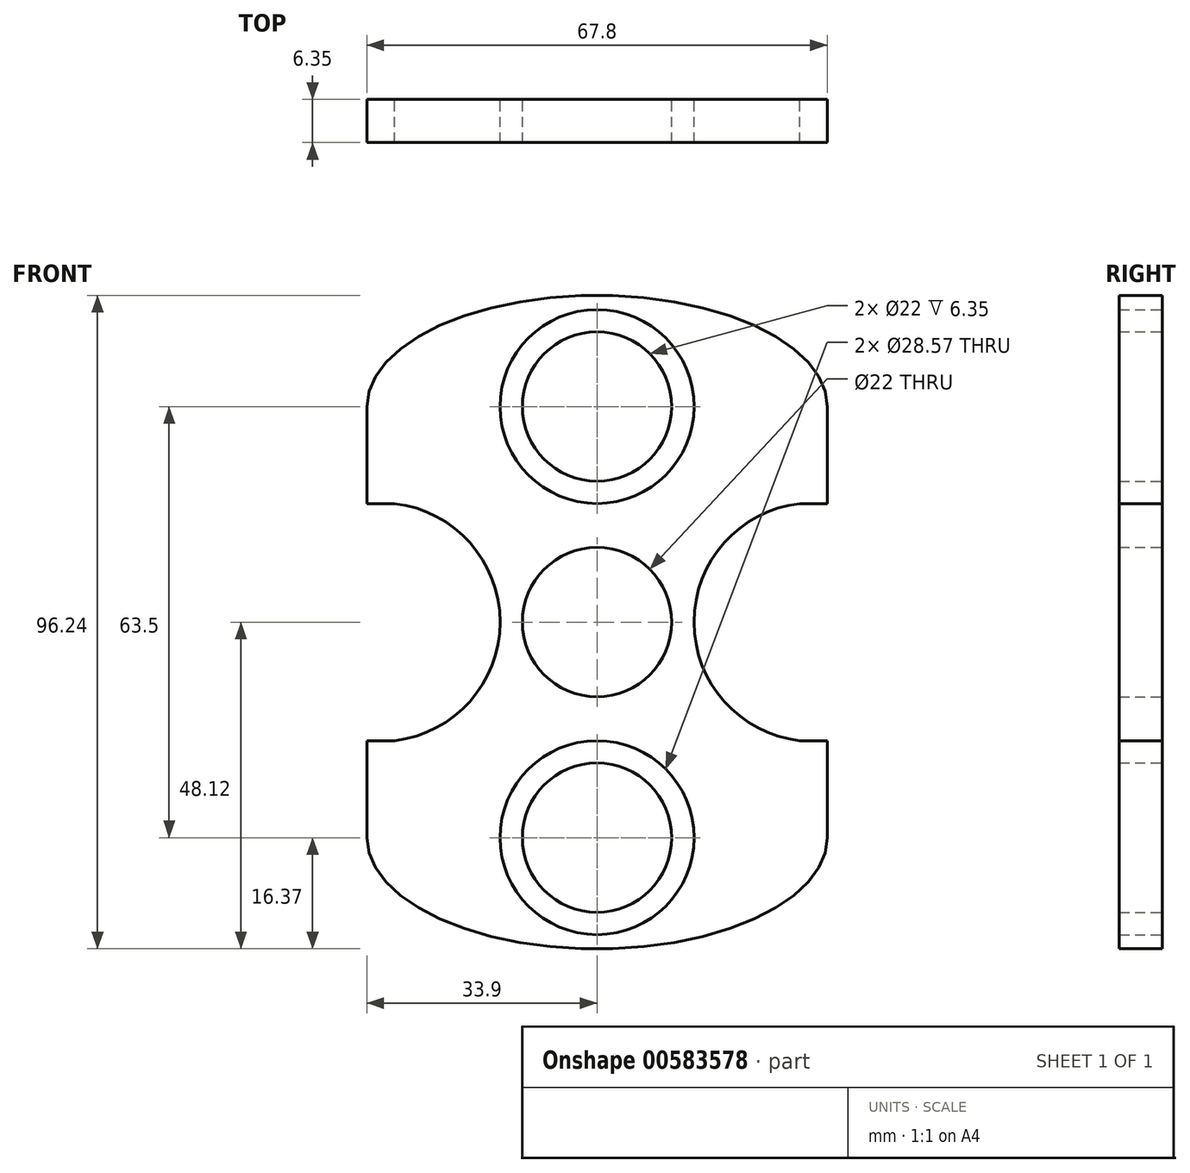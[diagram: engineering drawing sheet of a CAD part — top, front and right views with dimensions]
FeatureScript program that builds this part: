
annotation { "Feature Type Name" : "Feature", "Feature Type Description" : "" }
export const myFeature = defineFeature(function(context is Context, id is Id, definition is map)
    precondition{}
    {
        {
            var Q0;
            Q0=qCreatedBy(makeId("Front.planeOp"),FACE);
            var sketch = newSketch(context, id + "F0", { "sketchPlane" : qUnion([Q0])});
            skCircle(sketch, "E0", {"center": v(0, 0) * mm, "radius": 14.29 * mm});
            skCircle(sketch, "E1", {"center": v(0, 0) * mm, "radius": 11 * mm});
            skCircle(sketch, "E2", {"center": v(0, 31.75) * mm, "radius": 14.29 * mm});
            skCircle(sketch, "E3", {"center": v(0, 31.75) * mm, "radius": 11 * mm});
            skCircle(sketch, "E4.1.0", {"center": v(0, -31.75) * mm, "radius": 14.29 * mm});
            skCircle(sketch, "E4.1.1", {"center": v(0, -31.75) * mm, "radius": 11 * mm});
            skSolve(sketch);
        }
        {
            var Q0;
            Q0=qCreatedBy(makeId("Front.planeOp"),FACE);
            var sketch = newSketch(context, id + "F1", { "sketchPlane" : qUnion([Q0])});
            skCircle(sketch, "E5.0", {"center": v(0, 31.75) * mm, "radius": 14.29 * mm});
            skCircle(sketch, "E6.0", {"center": v(0, 31.75) * mm, "radius": 11 * mm});
            skCircle(sketch, "E7.0", {"center": v(0, 0) * mm, "radius": 14.29 * mm});
            skCircle(sketch, "E8.0", {"center": v(0, 0) * mm, "radius": 11 * mm});
            skCircle(sketch, "E9.0", {"center": v(0, -31.75) * mm, "radius": 14.29 * mm});
            skCircle(sketch, "E10.0", {"center": v(0, -31.75) * mm, "radius": 11 * mm});
            skEllipticalArc(sketch, "E11", {});
            skEllipticalArc(sketch, "E12.1.0", {});
            skLineSegment(sketch, "E13", {"start": v(-33.9, 31.75) * mm, "end": v(-33.9, 17.46) * mm});
            skLineSegment(sketch, "E14", {"start": v(-33.9, 17.46) * mm, "end": v(-29.83, 17.46) * mm});
            skLineSegment(sketch, "E15", {"start": v(33.9, 17.46) * mm, "end": v(33.9, 31.75) * mm});
            skLineSegment(sketch, "E16", {"start": v(14.29, 31.75) * mm, "end": v(11, 31.75) * mm});
            skLineSegment(sketch, "E17", {"start": v(-33.9, -31.75) * mm, "end": v(-33.9, -17.46) * mm});
            skLineSegment(sketch, "E18", {"start": v(-33.9, -17.46) * mm, "end": v(-29.83, -17.46) * mm});
            skLineSegment(sketch, "E19", {"start": v(33.9, -17.46) * mm, "end": v(33.9, -31.75) * mm});
            skArc(sketch, "E20", {"start": v(-33.9, -17.46) * mm, "mid": v(-14.29, 0) * mm, "end": v(-33.9, 17.46) * mm});
            skArc(sketch, "E21", {"start": v(33.9, 17.46) * mm, "mid": v(14.29, 0) * mm, "end": v(33.9, -17.46) * mm});
            skLineSegment(sketch, "E22.trimOffspring", {"start": v(29.83, -17.46) * mm, "end": v(33.9, -17.46) * mm});
            skLineSegment(sketch, "E23.trimOffspring", {"start": v(29.83, 17.46) * mm, "end": v(33.9, 17.46) * mm});
            skLineSegment(sketch, "E24.trimOffspring", {"start": v(-11, 31.75) * mm, "end": v(-14.29, 31.75) * mm});
            const initialGuessF1  = {"E11": [0, 0.03175, -1, 0, 0.033904947340488434, 0.016373396586444808, 3.141592653589793, 0], "E12.1.0": [0, -0.03175, 1, 0, 0.033904947340488434, 0.016373396586444808, 3.141592653589793, 0]};
            skSetInitialGuess(sketch, initialGuessF1);
            skSolve(sketch);
        }
        {
            var Q0;
            {var subQ0=sQuery(id+"F1.wireOp",EDGE,"E14");Q0=makeQuery(id+"F1.imprint","IMPRINT",FACE,{"disambiguationData":[TD([[makeQuery(id+"F1.imprint","IMPRINT",EDGE,{"derivedFrom":subQ0}),1.0]])]});}
            var Q1;
            {var subQ0=sQuery(id+"F1.wireOp",EDGE,"E18");Q1=makeQuery(id+"F1.imprint","IMPRINT",FACE,{"disambiguationData":[TD([[makeQuery(id+"F1.imprint","IMPRINT",EDGE,{"derivedFrom":subQ0}),-1.0]])]});}
            var Q2;
            {var subQ0=sQuery(id+"F1.wireOp",EDGE,"E23.trimOffspring");Q2=makeQuery(id+"F1.imprint","IMPRINT",FACE,{"disambiguationData":[TD([[makeQuery(id+"F1.imprint","IMPRINT",EDGE,{"derivedFrom":subQ0}),1.0]])]});}
            var Q3;
            {var subQ0=sQuery(id+"F1.wireOp",EDGE,"E22.trimOffspring");Q3=makeQuery(id+"F1.imprint","IMPRINT",FACE,{"disambiguationData":[TD([[makeQuery(id+"F1.imprint","IMPRINT",EDGE,{"derivedFrom":subQ0}),-1.0]])]});}
            var Q4;
            Q4=makeQuery(id+"F1.imprint","IMPRINT",FACE,{"disambiguationData":[TD([[makeQuery(id+"F1.imprint","IMPRINT",EDGE,{"derivedFrom":sQuery(id+"F1.wireOp",EDGE,"E8.0")}),-1.0]])]});
            var Q5;
            Q5=makeQuery(id+"F1.imprint","IMPRINT",FACE,{"disambiguationData":[TD([[makeQuery(id+"F1.imprint","IMPRINT",EDGE,{"derivedFrom":sQuery(id+"F1.wireOp",EDGE,"E9.0")}),-1.0]])]});
            var Q6;
            Q6=makeQuery(id+"F1.imprint","IMPRINT",FACE,{"disambiguationData":[TD([[makeQuery(id+"F1.imprint","IMPRINT",EDGE,{"derivedFrom":sQuery(id+"F1.wireOp",EDGE,"E11")}),1.0]])]});
            var Q7;
            Q7=makeQuery(id+"F0.imprint","IMPRINT",FACE,{"disambiguationData":[TD([[makeQuery(id+"F0.imprint","IMPRINT",EDGE,{"derivedFrom":sQuery(id+"F0.wireOp",EDGE,"E2")}),1.0]])]});
            var Q8;
            Q8=makeQuery(id+"F0.imprint","IMPRINT",FACE,{"disambiguationData":[TD([[makeQuery(id+"F0.imprint","IMPRINT",EDGE,{"derivedFrom":sQuery(id+"F0.wireOp",EDGE,"E4.1.0")}),1.0]])]});
            extrude(context, id + "F2", {"entities" : qUnion([Q0, Q1, Q2, Q3, Q4, Q5, Q6, Q7, Q8]), "depth" : 6.35 * mm, "offsetDistance" : 25.4 * mm});
        }
    });
